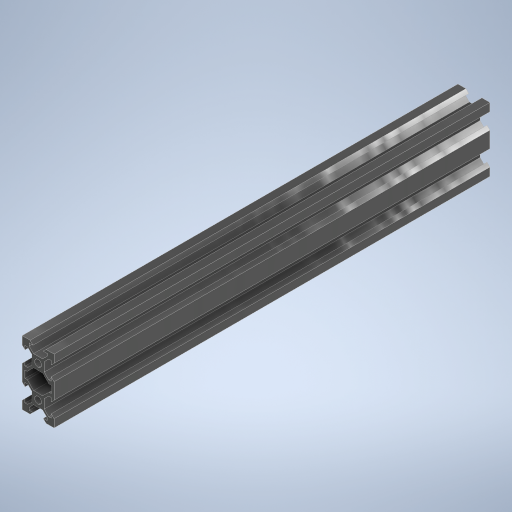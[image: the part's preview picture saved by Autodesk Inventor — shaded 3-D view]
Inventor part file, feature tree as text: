
AUTODESK INVENTOR PART (.ipt)
format: ipt  version: 2024.2 (Build 282272000, 272)  size: 416,768 bytes
history: native  units: mm
features: extrude x2, sketch x2, pattern_linear x1
ambient origin geometry x8: Origin, YZ Plane, XZ Plane, XY Plane, X Axis, Y Axis, Z Axis, Center Point
bodies: Solid1 (feature_tree)
feature tree (5):
  extrude  "ExtrusionModifier"  Depth=10.0mm
  pattern_linear  "Rectangular Pattern1"  Spacing1=4.4mm  [1 undecoded]
  extrude  "NoEdit"  TaperAngle=45.0deg  [1 undecoded]
  sketch  "Sketch1"  dims[d16=10.0mm d19=3.2mm]
  sketch  "Sketch2"  dims[d21=4.4mm d22=4.4mm d24=45.0deg d25=1.8mm d27=1.8mm d28=45.0deg d29=3.2mm d31=1.4mm d33=2.15mm d34=3.825mm d35=3.825mm d36=135.0deg d37=40.0mm d39=360.0deg d41=272.4mm d42=0.0mm d43=20.0mm d45=20.0mm d46=4.5mm d48=272.5mm d49=0.0mm d50=1.8mm d51=0.5mm d52=0.872665mm d53=0.5mm d54=0.872665mm]
note: 2 required parameter values undecoded (feature->parameter linkage not recoverable at this tier; creation-order binding heuristic only, values carry confidence <= 0.55)
